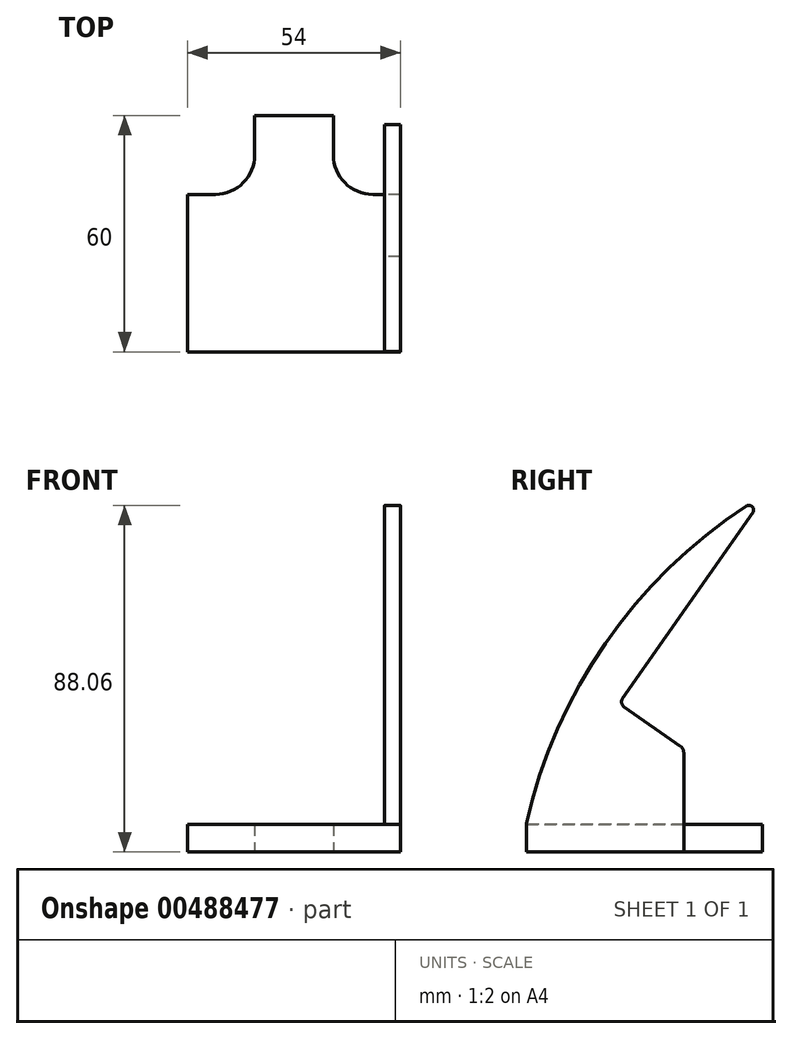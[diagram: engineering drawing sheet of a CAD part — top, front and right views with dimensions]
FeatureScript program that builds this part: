
annotation { "Feature Type Name" : "Feature", "Feature Type Description" : "" }
export const myFeature = defineFeature(function(context is Context, id is Id, definition is map)
    precondition{}
    {
        {
            var Q0;
            Q0=qCreatedBy(makeId("Top.planeOp"),FACE);
            var sketch = newSketch(context, id + "F0", { "sketchPlane" : qUnion([Q0])});
            skLineSegment(sketch, "E0.bottom", {"start": v(27, -20) * mm, "end": v(-27, -20) * mm});
            skLineSegment(sketch, "E0.top", {"start": v(27, 20) * mm, "end": v(10, 20) * mm});
            skLineSegment(sketch, "E0.left", {"start": v(27, -20) * mm, "end": v(27, 20) * mm});
            skLineSegment(sketch, "E0.right", {"start": v(-27, -20) * mm, "end": v(-27, 20) * mm});
            skPoint(sketch, "E0.middle", {"position": v(0, 0) * mm});
            skLineSegment(sketch, "E1.top", {"start": v(10, 40) * mm, "end": v(-10, 40) * mm});
            skLineSegment(sketch, "E1.left", {"start": v(10, 20) * mm, "end": v(10, 40) * mm});
            skLineSegment(sketch, "E1.right", {"start": v(-10, 20) * mm, "end": v(-10, 40) * mm});
            skPoint(sketch, "E1.middle", {"position": v(0, 20) * mm});
            skPoint(sketch, "E1.bottom.end.orphan", {"position": v(-10, 0) * mm});
            skPoint(sketch, "E1.bottom.start.orphan", {"position": v(10, 0) * mm});
            skLineSegment(sketch, "E2.trimOffspring", {"start": v(-10, 20) * mm, "end": v(-27, 20) * mm});
            skSolve(sketch);
        }
        {
            var Q0;
            Q0=makeQuery(id+"F0.imprint","IMPRINT",FACE,{"disambiguationData":[TD([[makeQuery(id+"F0.imprint","IMPRINT",EDGE,{"derivedFrom":sQuery(id+"F0.wireOp",EDGE,"E0.bottom")}),-1.0]])]});
            extrude(context, id + "F1", {"entities" : qUnion([Q0]), "depth" : 7 * mm});
        }
        {
            var Q0;
            Q0=makeQuery(id+"F1.opExtrude","SWEPT_EDGE",EDGE,{"disambiguationData":[OSD([sQuery(id+"F0.wireOp",EDGE,"E0.top"),sQuery(id+"F0.wireOp",EDGE,"E1.left")])]});
            var Q1;
            Q1=makeQuery(id+"F1.opExtrude","SWEPT_EDGE",EDGE,{"disambiguationData":[OSD([sQuery(id+"F0.wireOp",EDGE,"E1.right"),sQuery(id+"F0.wireOp",EDGE,"E2.trimOffspring")])]});
            fillet(context, id + "F2", {"entities" : qUnion([Q0, Q1]), "radius" : 10 * mm, "tangentPropagation" : true, "allowEdgeOverflow" : false});
        }
        {
            var Q0;
            Q0=qCreatedBy(makeId("Right.planeOp"),FACE);
            cPlane(context, id + "F3", {"entities" : qUnion([Q0]), "cplaneType" : CPlaneType.OFFSET, "offset" : 23 * mm, "width" : 150 * mm, "height" : 150 * mm});
        }
        {
            var Q0;
            Q0=qCreatedBy(id+"F3.planeOp",FACE);
            var sketch = newSketch(context, id + "F4", { "sketchPlane" : qUnion([Q0])});
            skLineSegment(sketch, "E3.bottom", {"start": v(20, 0) * mm, "end": v(-20, 0) * mm});
            skLineSegment(sketch, "E3.top", {"start": v(20, 7) * mm, "end": v(-20, 7) * mm});
            skLineSegment(sketch, "E3.left", {"start": v(20, 0) * mm, "end": v(20, 7) * mm});
            skLineSegment(sketch, "E3.right", {"start": v(-20, 0) * mm, "end": v(-20, 6.78) * mm});
            skLineSegment(sketch, "E4", {"start": v(20, 7) * mm, "end": v(20, 25.2) * mm});
            skLineSegment(sketch, "E5", {"start": v(19.15, 26.85) * mm, "end": v(4.85, 36.86) * mm});
            skLineSegment(sketch, "E6", {"start": v(4.48, 38.95) * mm, "end": v(37.54, 86.17) * mm});
            skArc(sketch, "E7", {"start": v(35.9, 87.86) * mm, "mid": v(0.08, 53.01) * mm, "end": v(-19.95, 7.22) * mm});
            skPoint(sketch, "E8.visualSharp", {"position": v(40.9, 90.97) * mm});
            skArc(sketch, "E8.filletArc", {"start": v(37.54, 86.17) * mm, "mid": v(37.42, 87.7) * mm, "end": v(35.9, 87.86) * mm});
            skPoint(sketch, "E9.visualSharp", {"position": v(3.62, 37.72) * mm});
            skArc(sketch, "E9.filletArc", {"start": v(4.48, 38.95) * mm, "mid": v(4.23, 37.83) * mm, "end": v(4.85, 36.86) * mm});
            skPoint(sketch, "E10.visualSharp", {"position": v(20, 26.25) * mm});
            skArc(sketch, "E10.filletArc", {"start": v(20, 25.2) * mm, "mid": v(19.77, 26.13) * mm, "end": v(19.15, 26.85) * mm});
            skPoint(sketch, "E11.visualSharp", {"position": v(-20, 7) * mm});
            skArc(sketch, "E11.filletArc", {"start": v(-19.95, 7.22) * mm, "mid": v(-19.99, 7) * mm, "end": v(-20, 6.78) * mm});
            skSolve(sketch);
        }
        {
            var Q0;
            {var subQ0=sQuery(id+"F4.wireOp",EDGE,"E4");Q0=makeQuery(id+"F4.imprint","IMPRINT",FACE,{"disambiguationData":[TD([[makeQuery(id+"F4.imprint","IMPRINT",EDGE,{"derivedFrom":subQ0}),1.0]])]});}
            extrude(context, id + "F5", {"entities" : qUnion([Q0]), "operationType" : NewBodyOperationType.ADD, "depth" : 4 * mm});
        }
    });
